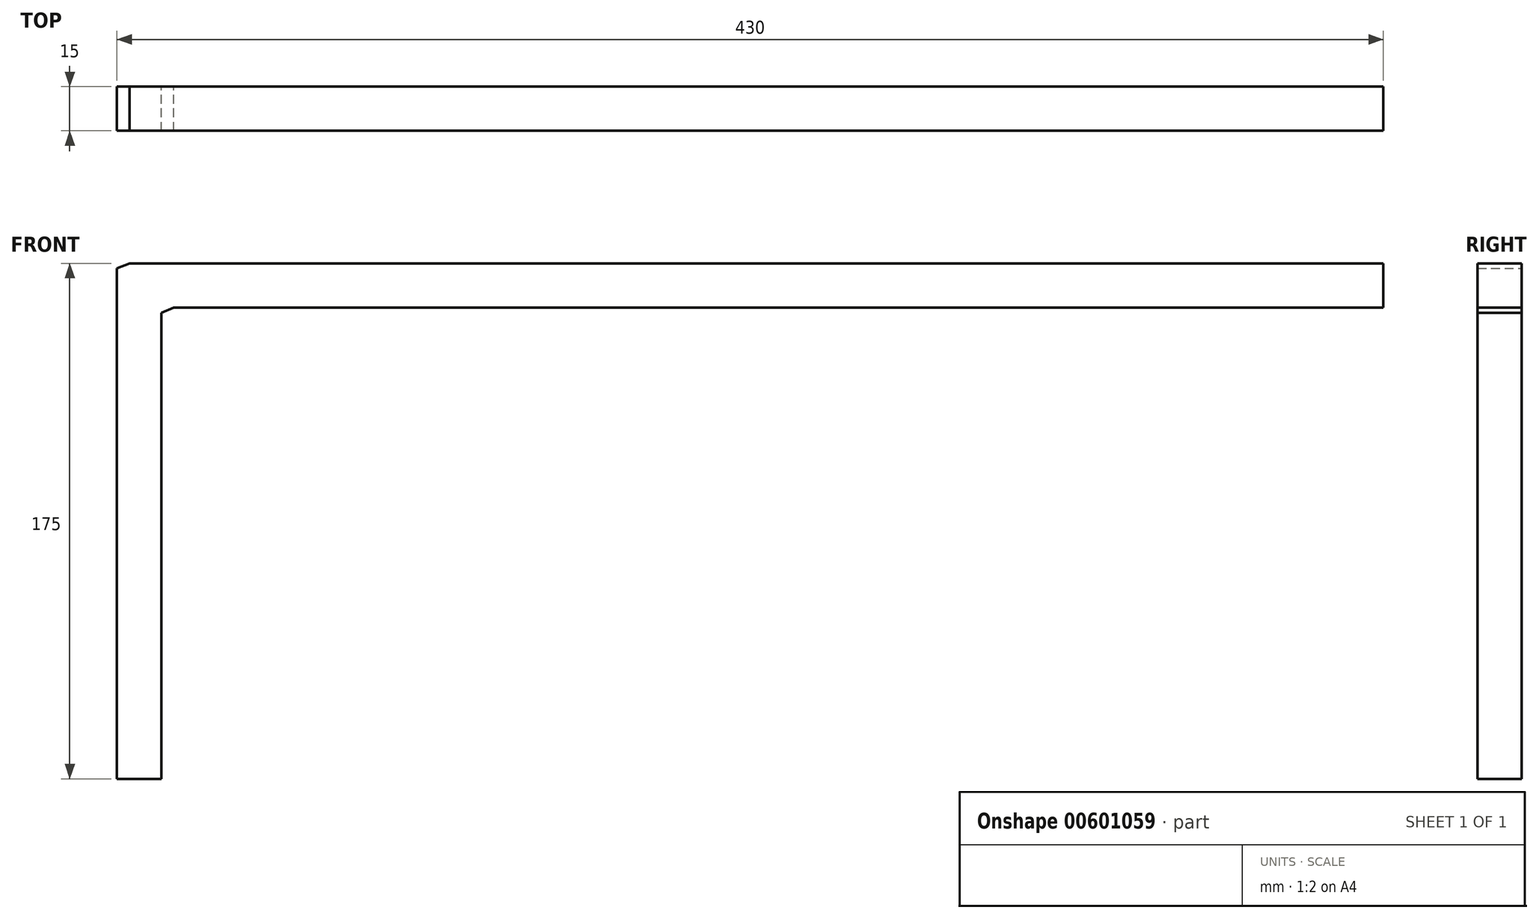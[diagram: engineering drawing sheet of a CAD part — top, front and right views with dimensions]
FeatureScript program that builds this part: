
annotation { "Feature Type Name" : "Feature", "Feature Type Description" : "" }
export const myFeature = defineFeature(function(context is Context, id is Id, definition is map)
    precondition{}
    {
        {
            var Q0;
            Q0=qCreatedBy(makeId("Front.planeOp"),FACE);
            var sketch = newSketch(context, id + "F0", { "sketchPlane" : qUnion([Q0])});
            skLineSegment(sketch, "E0", {"start": v(0, 0) * mm, "end": v(0, 173.25) * mm});
            skLineSegment(sketch, "E1", {"start": v(4.3, 175) * mm, "end": v(430, 175) * mm});
            skLineSegment(sketch, "E2", {"start": v(430, 175) * mm, "end": v(430, 160) * mm});
            skLineSegment(sketch, "E3", {"start": v(430, 160) * mm, "end": v(19.3, 160) * mm});
            skLineSegment(sketch, "E4", {"start": v(15, 158.25) * mm, "end": v(15, 0) * mm});
            skLineSegment(sketch, "E5", {"start": v(15, 0) * mm, "end": v(0, 0) * mm});
            skPoint(sketch, "E6.visualSharp", {"position": v(0, 175) * mm});
            skPoint(sketch, "E7.visualSharp", {"position": v(15, 160) * mm});
            skLineSegment(sketch, "E8", {"start": v(0, 173.25) * mm, "end": v(4.3, 175) * mm});
            skLineSegment(sketch, "E9", {"start": v(15, 158.25) * mm, "end": v(19.3, 160) * mm});
            skSolve(sketch);
        }
        {
            var Q0;
            Q0=makeQuery(id+"F0.imprint","IMPRINT",FACE,{"disambiguationData":[TD([[makeQuery(id+"F0.imprint","IMPRINT",EDGE,{"derivedFrom":sQuery(id+"F0.wireOp",EDGE,"E0")}),-1.0]])]});
            extrude(context, id + "F1", {"entities" : qUnion([Q0]), "depth" : 15 * mm, "offsetDistance" : 25 * mm});
        }
    });
